# Revit family: CADS_Vent-Axia_Lo-CarbonSentinelKineticCookerHood
name_source: partatom
category: Mechanical Equipment
revit_build: Autodesk Revit 2015 (Build: 20140223_1515(x64)
units: mm (PartAtom-declared; Revit-internal decimal feet)

## types (4) — shared parameters
Apparent Load = 690 VA
AssetType = Fixed
Category = Pr_60_60_36:Heat recovery distribution equipment
Color = White
Description = Lo-Carbon Sentinel Kinetic Cooker Hood
DurationUnit = year
ExpectedLife = 20
IfcExportAs = IfcAirToAirHeatRecoveryType
IfcExportType = USERDEFINED
Manufacturer = Vent-Axia Limited
Material = ABS Plastic
Name = MVHR Unit
NominalHeight = 550 mm
NominalLength = 550 mm
NominalWidth = 285 mm  [stored 0.935039 ft]
NumberOfPoles = 1
RatedCurrent = 3 A
RatedVoltage = 230 V
Shape = Rectangular
Size = 285mm x 550mm x 550mm 
285mm x 550mm x 550mm
SpigotConnLength = 160 mm  [stored 0.524934 ft]
SpigotConnWidth = 120 mm  [stored 0.393701 ft]
SpigotCrsLength = 360 mm  [stored 1.1811 ft]
SpigotCrsWidth = 140 mm  [stored 0.459318 ft]
SpigotDiameter = 125 mm  [stored 0.410105 ft]
SpigotHeight = 90 mm  [stored 0.295276 ft]
SpigotOffset = 95 mm  [stored 0.31168 ft]
Version = 1.0
WarrantyDurationLabor = 2
WarrantyDurationMotors = 5
WarrantyDurationParts = 2
WarrantyDurationUnit = year

## per-type parameters (varying)
| type | LeftHand | Model | ModelNumber | ModelReference | RightHand |
| CWH Right Hand | No | Kinetic Cooker Hood Unit CWHR | 438222 | Kinetic Cooker Hood Unit CWHR | Yes |
| CWH Left Hand | Yes | Kinetic Cooker Hood Unit CWHL | 446756 | Kinetic Cooker Hood Unit CWHL | No |
| CSH Left Hand | Yes | Kinetic Cooker Hood Unit CSHL | 446757 | Kinetic Cooker Hood Unit CSHL | No |
| CSH Right Hand | No | Kinetic Cooker Hood Unit CSHR | 446759 | Kinetic Cooker Hood Unit CSHR | Yes |

note: [stored X ft] marks values corroborated as IEEE doubles in the binary element streams (Revit-internal decimal feet)

## geometry (parser evidence)
native form markers: Sweep x17
no freeform markers — native parametric forms only
